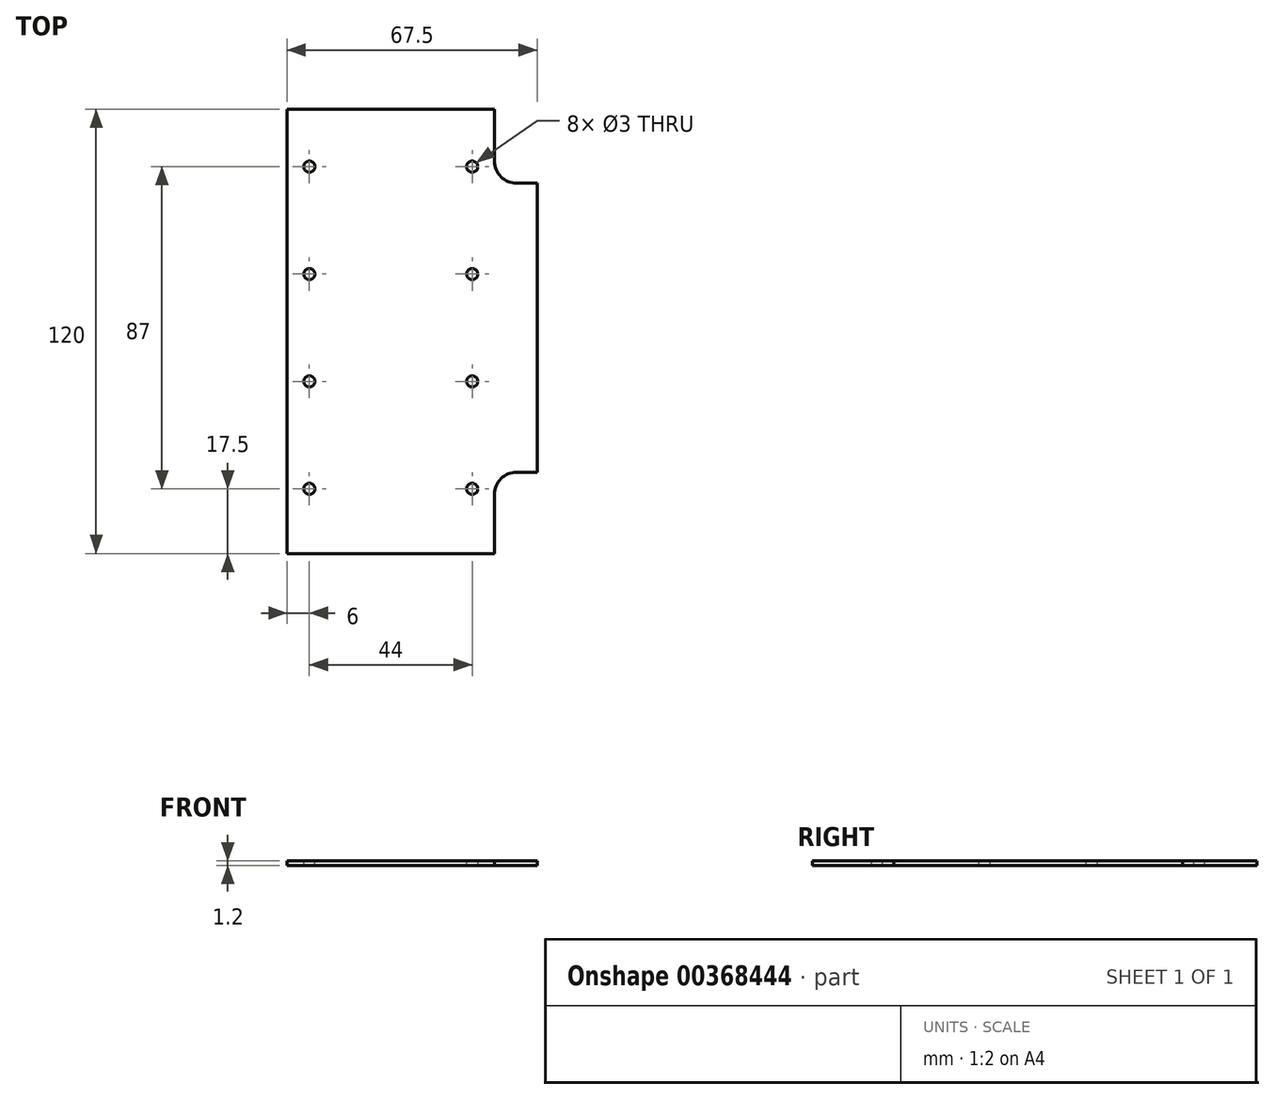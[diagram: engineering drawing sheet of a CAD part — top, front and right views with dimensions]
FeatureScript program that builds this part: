
annotation { "Feature Type Name" : "Feature", "Feature Type Description" : "" }
export const myFeature = defineFeature(function(context is Context, id is Id, definition is map)
    precondition{}
    {
        {
            var Q0;
            Q0=qCreatedBy(makeId("Top.planeOp"),FACE);
            var sketch = newSketch(context, id + "F0", { "sketchPlane" : qUnion([Q0])});
            skLineSegment(sketch, "E0.bottom", {"start": v(0, 120) * mm, "end": v(56, 120) * mm});
            skLineSegment(sketch, "E0.top", {"start": v(0, 0) * mm, "end": v(56, 0) * mm});
            skLineSegment(sketch, "E0.left", {"start": v(0, 120) * mm, "end": v(0, 0) * mm});
            skLineSegment(sketch, "E0.right", {"start": v(56, 120) * mm, "end": v(56, 0) * mm});
            skPoint(sketch, "E0.middle", {"position": v(0, 0) * mm});
            skCircle(sketch, "E1", {"center": v(-6, 16) * mm, "radius": 4.8 * mm});
            skCircle(sketch, "E2", {"center": v(-6, 106) * mm, "radius": 4.8 * mm});
            skCircle(sketch, "E3", {"center": v(62, 106) * mm, "radius": 4.8 * mm});
            skCircle(sketch, "E4", {"center": v(62, 16) * mm, "radius": 4.8 * mm});
            skArc(sketch, "E5", {"start": v(56, 106) * mm, "mid": v(57.76, 101.76) * mm, "end": v(62, 100) * mm});
            skLineSegment(sketch, "E6", {"start": v(62, 100) * mm, "end": v(67.5, 100) * mm});
            skLineSegment(sketch, "E7", {"start": v(67.5, 100) * mm, "end": v(67.5, 22) * mm});
            skLineSegment(sketch, "E8", {"start": v(67.5, 22) * mm, "end": v(62, 22) * mm});
            skArc(sketch, "E9", {"start": v(62, 22) * mm, "mid": v(57.76, 20.24) * mm, "end": v(56, 16) * mm});
            skLineSegment(sketch, "E10", {"start": v(-6, 106) * mm, "end": v(0, 106) * mm});
            skLineSegment(sketch, "E11", {"start": v(62, 106) * mm, "end": v(56, 106) * mm});
            skSolve(sketch);
        }
        {
            var Q0;
            {var subQ3=sQuery(id+"F0.wireOp",EDGE,"E0.bottom");Q0=makeQuery(id+"F0.imprint","IMPRINT",FACE,{"disambiguationData":[TD([[makeQuery(id+"F0.imprint","IMPRINT",EDGE,{"derivedFrom":subQ3}),-1.0]])]});}
            var Q1;
            {var subQ5=sQuery(id+"F0.wireOp",EDGE,"iA3OclCX-mQHG-l4Gt-ZmRm-Y9ssZ7GcRiAx");Q1=makeQuery(id+"F0.imprint","IMPRINT",FACE,{"disambiguationData":[TD([[makeQuery(id+"F0.imprint","IMPRINT",EDGE,{"derivedFrom":subQ5}),-1.0]])]});}
            var Q2;
            {var subQ4=sQuery(id+"F0.wireOp",EDGE,"iA3OclCX-mQHG-l4Gt-ZmRm-Y9ssZ7GcRiAx");Q2=makeQuery(id+"F0.imprint","IMPRINT",FACE,{"disambiguationData":[TD([[makeQuery(id+"F0.imprint","IMPRINT",EDGE,{"derivedFrom":subQ4}),1.0]])]});}
            var Q3;
            {var subQ3=sQuery(id+"F0.wireOp",EDGE,"pLjdYPaW-lVR8-Q6IO-74R2-BZIg2K0lFj3H");Q3=makeQuery(id+"F0.imprint","IMPRINT",FACE,{"disambiguationData":[TD([[makeQuery(id+"F0.imprint","IMPRINT",EDGE,{"derivedFrom":subQ3}),-1.0]])]});}
            var Q4;
            {var subQ3=sQuery(id+"F0.wireOp",EDGE,"pLjdYPaW-lVR8-Q6IO-74R2-BZIg2K0lFj3H");Q4=makeQuery(id+"F0.imprint","IMPRINT",FACE,{"disambiguationData":[TD([[makeQuery(id+"F0.imprint","IMPRINT",EDGE,{"derivedFrom":subQ3}),1.0]])]});}
            var Q5;
            {var subQ0=sQuery(id+"F0.wireOp",EDGE,"E5");Q5=makeQuery(id+"F0.imprint","IMPRINT",FACE,{"disambiguationData":[TD([[makeQuery(id+"F0.imprint","IMPRINT",EDGE,{"derivedFrom":subQ0}),-1.0]])]});}
            extrude(context, id + "F1", {"entities" : qUnion([Q0, Q1, Q2, Q3, Q4, Q5]), "endBound" : BoundingType.SYMMETRIC, "depth" : 1.2 * mm});
        }
        {
            var Q0;
            Q0=makeQuery(id+"F1.opExtrude","CAP_FACE",FACE,{"disambiguationData":[OSD([sQuery(id+"F0.wireOp",EDGE,"E0.bottom"),sQuery(id+"F0.wireOp",EDGE,"E0.top"),sQuery(id+"F0.wireOp",EDGE,"E0.left"),sQuery(id+"F0.wireOp",EDGE,"E0.right")])],"isStart":false});
            var sketch = newSketch(context, id + "F2", { "sketchPlane" : qUnion([Q0])});
            skLineSegment(sketch, "E12", {"start": v(6, 104.5) * mm, "end": v(50, 104.5) * mm});
            skLineSegment(sketch, "E13", {"start": v(50, 75.5) * mm, "end": v(50, 46.5) * mm});
            skLineSegment(sketch, "E14", {"start": v(50, 104.5) * mm, "end": v(50, 75.5) * mm});
            skLineSegment(sketch, "E15", {"start": v(50, 46.5) * mm, "end": v(50, 17.5) * mm});
            skLineSegment(sketch, "E16", {"start": v(50, 17.5) * mm, "end": v(6, 17.5) * mm});
            skLineSegment(sketch, "E17", {"start": v(6, 17.5) * mm, "end": v(6, 46.5) * mm});
            skLineSegment(sketch, "E18", {"start": v(6, 46.5) * mm, "end": v(6, 75.5) * mm});
            skLineSegment(sketch, "E19", {"start": v(6, 104.5) * mm, "end": v(6, 75.5) * mm});
            skCircle(sketch, "E20", {"center": v(6, 104.5) * mm, "radius": 1.5 * mm});
            skCircle(sketch, "E21", {"center": v(50, 104.5) * mm, "radius": 1.5 * mm});
            skCircle(sketch, "E22", {"center": v(50, 75.5) * mm, "radius": 1.5 * mm});
            skCircle(sketch, "E23", {"center": v(50, 46.5) * mm, "radius": 1.5 * mm});
            skCircle(sketch, "E24", {"center": v(50, 17.5) * mm, "radius": 1.5 * mm});
            skCircle(sketch, "E25", {"center": v(6, 17.5) * mm, "radius": 1.5 * mm});
            skCircle(sketch, "E26", {"center": v(6, 46.5) * mm, "radius": 1.5 * mm});
            skCircle(sketch, "E27", {"center": v(6, 75.5) * mm, "radius": 1.5 * mm});
            skSolve(sketch);
        }
        {
            var Q0;
            {var subQ0=sQuery(id+"F2.wireOp",EDGE,"E19");var subQ1=sQuery(id+"F2.wireOp",EDGE,"E12");var subQ2=makeQuery(id+"F2.imprint","INTERSECT",VERTEX,{"derivedFrom":[subQ1,subQ0]});Q0=makeQuery(id+"F2.imprint","IMPRINT",FACE,{"disambiguationData":[TD([[makeQuery(id+"F2.imprint","IMPRINT",EDGE,{"disambiguationData":[TD([[subQ2,-1.0]])],"derivedFrom":subQ1}),1.0]])]});}
            var Q1;
            {var subQ0=sQuery(id+"F2.wireOp",EDGE,"E19");var subQ1=sQuery(id+"F2.wireOp",EDGE,"E12");var subQ2=makeQuery(id+"F2.imprint","INTERSECT",VERTEX,{"derivedFrom":[subQ1,subQ0]});Q1=makeQuery(id+"F2.imprint","IMPRINT",FACE,{"disambiguationData":[TD([[makeQuery(id+"F2.imprint","IMPRINT",EDGE,{"disambiguationData":[TD([[subQ2,-1.0]])],"derivedFrom":subQ1}),-1.0]])]});}
            var Q2;
            {var subQ0=sQuery(id+"F2.wireOp",EDGE,"E14");var subQ1=sQuery(id+"F2.wireOp",EDGE,"E12");var subQ2=makeQuery(id+"F2.imprint","INTERSECT",VERTEX,{"derivedFrom":[subQ1,subQ0]});Q2=makeQuery(id+"F2.imprint","IMPRINT",FACE,{"disambiguationData":[TD([[makeQuery(id+"F2.imprint","IMPRINT",EDGE,{"disambiguationData":[TD([[subQ2,1.0]])],"derivedFrom":subQ1}),1.0]])]});}
            var Q3;
            {var subQ0=sQuery(id+"F2.wireOp",EDGE,"E14");var subQ1=sQuery(id+"F2.wireOp",EDGE,"E12");var subQ2=makeQuery(id+"F2.imprint","INTERSECT",VERTEX,{"derivedFrom":[subQ1,subQ0]});Q3=makeQuery(id+"F2.imprint","IMPRINT",FACE,{"disambiguationData":[TD([[makeQuery(id+"F2.imprint","IMPRINT",EDGE,{"disambiguationData":[TD([[subQ2,1.0]])],"derivedFrom":subQ1}),-1.0]])]});}
            var Q4;
            {var subQ0=sQuery(id+"F2.wireOp",EDGE,"E14");var subQ1=sQuery(id+"F2.wireOp",EDGE,"E13");var subQ2=makeQuery(id+"F2.imprint","INTERSECT",VERTEX,{"derivedFrom":[subQ1,subQ0]});Q4=makeQuery(id+"F2.imprint","IMPRINT",FACE,{"disambiguationData":[TD([[makeQuery(id+"F2.imprint","IMPRINT",EDGE,{"disambiguationData":[TD([[subQ2,-1.0]])],"derivedFrom":subQ1}),1.0]])]});}
            var Q5;
            {var subQ0=sQuery(id+"F2.wireOp",EDGE,"E14");var subQ1=sQuery(id+"F2.wireOp",EDGE,"E13");var subQ2=makeQuery(id+"F2.imprint","INTERSECT",VERTEX,{"derivedFrom":[subQ1,subQ0]});Q5=makeQuery(id+"F2.imprint","IMPRINT",FACE,{"disambiguationData":[TD([[makeQuery(id+"F2.imprint","IMPRINT",EDGE,{"disambiguationData":[TD([[subQ2,-1.0]])],"derivedFrom":subQ1}),-1.0]])]});}
            var Q6;
            {var subQ0=sQuery(id+"F2.wireOp",EDGE,"E15");var subQ1=sQuery(id+"F2.wireOp",EDGE,"E13");var subQ2=makeQuery(id+"F2.imprint","INTERSECT",VERTEX,{"derivedFrom":[subQ1,subQ0]});Q6=makeQuery(id+"F2.imprint","IMPRINT",FACE,{"disambiguationData":[TD([[makeQuery(id+"F2.imprint","IMPRINT",EDGE,{"disambiguationData":[TD([[subQ2,1.0]])],"derivedFrom":subQ1}),1.0]])]});}
            var Q7;
            {var subQ0=sQuery(id+"F2.wireOp",EDGE,"E15");var subQ1=sQuery(id+"F2.wireOp",EDGE,"E13");var subQ2=makeQuery(id+"F2.imprint","INTERSECT",VERTEX,{"derivedFrom":[subQ1,subQ0]});Q7=makeQuery(id+"F2.imprint","IMPRINT",FACE,{"disambiguationData":[TD([[makeQuery(id+"F2.imprint","IMPRINT",EDGE,{"disambiguationData":[TD([[subQ2,1.0]])],"derivedFrom":subQ1}),-1.0]])]});}
            var Q8;
            {var subQ0=sQuery(id+"F2.wireOp",EDGE,"E16");var subQ1=sQuery(id+"F2.wireOp",EDGE,"E15");var subQ2=makeQuery(id+"F2.imprint","INTERSECT",VERTEX,{"derivedFrom":[subQ1,subQ0]});Q8=makeQuery(id+"F2.imprint","IMPRINT",FACE,{"disambiguationData":[TD([[makeQuery(id+"F2.imprint","IMPRINT",EDGE,{"disambiguationData":[TD([[subQ2,1.0]])],"derivedFrom":subQ1}),1.0]])]});}
            var Q9;
            {var subQ0=sQuery(id+"F2.wireOp",EDGE,"E16");var subQ1=sQuery(id+"F2.wireOp",EDGE,"E15");var subQ2=makeQuery(id+"F2.imprint","INTERSECT",VERTEX,{"derivedFrom":[subQ1,subQ0]});Q9=makeQuery(id+"F2.imprint","IMPRINT",FACE,{"disambiguationData":[TD([[makeQuery(id+"F2.imprint","IMPRINT",EDGE,{"disambiguationData":[TD([[subQ2,1.0]])],"derivedFrom":subQ1}),-1.0]])]});}
            var Q10;
            {var subQ0=sQuery(id+"F2.wireOp",EDGE,"E17");var subQ1=sQuery(id+"F2.wireOp",EDGE,"E16");var subQ2=makeQuery(id+"F2.imprint","INTERSECT",VERTEX,{"derivedFrom":[subQ1,subQ0]});Q10=makeQuery(id+"F2.imprint","IMPRINT",FACE,{"disambiguationData":[TD([[makeQuery(id+"F2.imprint","IMPRINT",EDGE,{"disambiguationData":[TD([[subQ2,1.0]])],"derivedFrom":subQ1}),1.0]])]});}
            var Q11;
            {var subQ0=sQuery(id+"F2.wireOp",EDGE,"E17");var subQ1=sQuery(id+"F2.wireOp",EDGE,"E16");var subQ2=makeQuery(id+"F2.imprint","INTERSECT",VERTEX,{"derivedFrom":[subQ1,subQ0]});Q11=makeQuery(id+"F2.imprint","IMPRINT",FACE,{"disambiguationData":[TD([[makeQuery(id+"F2.imprint","IMPRINT",EDGE,{"disambiguationData":[TD([[subQ2,1.0]])],"derivedFrom":subQ1}),-1.0]])]});}
            var Q12;
            {var subQ0=sQuery(id+"F2.wireOp",EDGE,"E18");var subQ1=sQuery(id+"F2.wireOp",EDGE,"E17");var subQ2=makeQuery(id+"F2.imprint","INTERSECT",VERTEX,{"derivedFrom":[subQ1,subQ0]});Q12=makeQuery(id+"F2.imprint","IMPRINT",FACE,{"disambiguationData":[TD([[makeQuery(id+"F2.imprint","IMPRINT",EDGE,{"disambiguationData":[TD([[subQ2,1.0]])],"derivedFrom":subQ1}),1.0]])]});}
            var Q13;
            {var subQ0=sQuery(id+"F2.wireOp",EDGE,"E18");var subQ1=sQuery(id+"F2.wireOp",EDGE,"E17");var subQ2=makeQuery(id+"F2.imprint","INTERSECT",VERTEX,{"derivedFrom":[subQ1,subQ0]});Q13=makeQuery(id+"F2.imprint","IMPRINT",FACE,{"disambiguationData":[TD([[makeQuery(id+"F2.imprint","IMPRINT",EDGE,{"disambiguationData":[TD([[subQ2,1.0]])],"derivedFrom":subQ1}),-1.0]])]});}
            var Q14;
            {var subQ0=sQuery(id+"F2.wireOp",EDGE,"E19");var subQ1=sQuery(id+"F2.wireOp",EDGE,"E18");var subQ2=makeQuery(id+"F2.imprint","INTERSECT",VERTEX,{"derivedFrom":[subQ1,subQ0]});Q14=makeQuery(id+"F2.imprint","IMPRINT",FACE,{"disambiguationData":[TD([[makeQuery(id+"F2.imprint","IMPRINT",EDGE,{"disambiguationData":[TD([[subQ2,1.0]])],"derivedFrom":subQ1}),1.0]])]});}
            var Q15;
            {var subQ0=sQuery(id+"F2.wireOp",EDGE,"E19");var subQ1=sQuery(id+"F2.wireOp",EDGE,"E18");var subQ2=makeQuery(id+"F2.imprint","INTERSECT",VERTEX,{"derivedFrom":[subQ1,subQ0]});Q15=makeQuery(id+"F2.imprint","IMPRINT",FACE,{"disambiguationData":[TD([[makeQuery(id+"F2.imprint","IMPRINT",EDGE,{"disambiguationData":[TD([[subQ2,1.0]])],"derivedFrom":subQ1}),-1.0]])]});}
            extrude(context, id + "F3", {"entities" : qUnion([Q0, Q1, Q2, Q3, Q4, Q5, Q6, Q7, Q8, Q9, Q10, Q11, Q12, Q13, Q14, Q15]), "operationType" : NewBodyOperationType.REMOVE, "endBound" : BoundingType.THROUGH_ALL, "oppositeDirection" : true, "depth" : 25 * mm});
        }
    });
